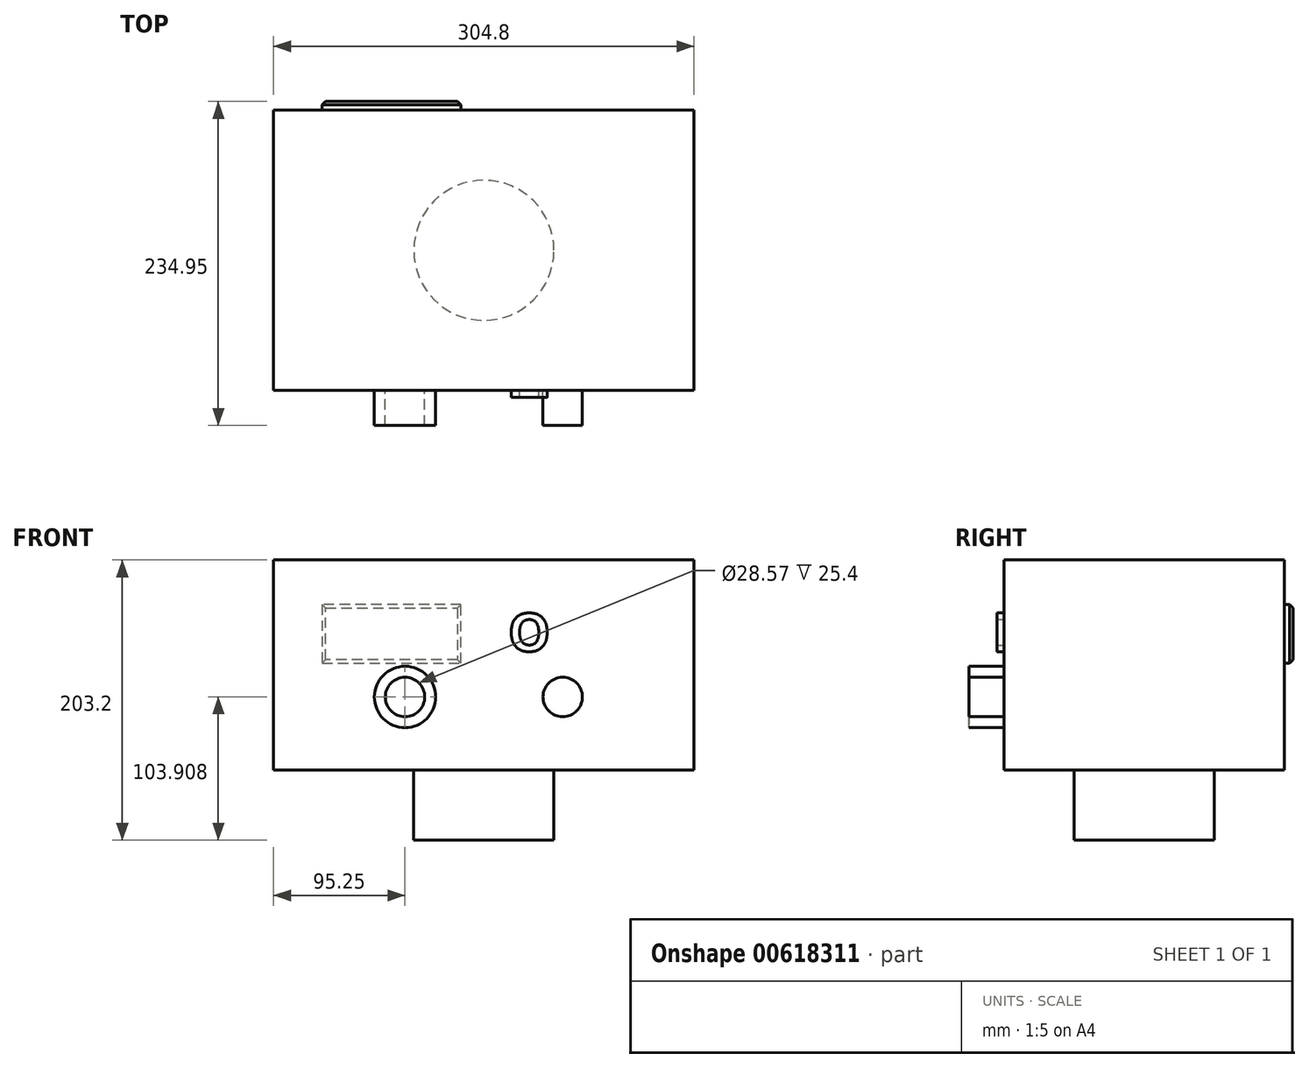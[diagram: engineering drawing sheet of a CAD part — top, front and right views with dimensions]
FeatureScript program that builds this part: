
annotation { "Feature Type Name" : "Feature", "Feature Type Description" : "" }
export const myFeature = defineFeature(function(context is Context, id is Id, definition is map)
    precondition{}
    {
        {
            var Q0;
            Q0=qCreatedBy(makeId("Top.planeOp"),FACE);
            var sketch = newSketch(context, id + "F0", { "sketchPlane" : qUnion([Q0])});
            skLineSegment(sketch, "E0", {"start": v(0, 0) * mm, "end": v(152.4, 0) * mm});
            skLineSegment(sketch, "E1", {"start": v(0, 0) * mm, "end": v(0, 101.6) * mm});
            skLineSegment(sketch, "E2", {"start": v(0, 0) * mm, "end": v(0, -101.6) * mm});
            skLineSegment(sketch, "E3", {"start": v(0, 101.6) * mm, "end": v(152.4, 101.6) * mm});
            skLineSegment(sketch, "E4", {"start": v(0, 0) * mm, "end": v(36.33, -35.5) * mm});
            skCircle(sketch, "E5", {"center": v(0, 0) * mm, "radius": 50.8 * mm});
            skLineSegment(sketch, "E6.bottom", {"start": v(152.4, 101.6) * mm, "end": v(-152.4, 101.6) * mm});
            skLineSegment(sketch, "E6.top", {"start": v(152.4, -101.6) * mm, "end": v(-152.4, -101.6) * mm});
            skLineSegment(sketch, "E6.left", {"start": v(152.4, 101.6) * mm, "end": v(152.4, -101.6) * mm});
            skLineSegment(sketch, "E6.right", {"start": v(-152.4, 101.6) * mm, "end": v(-152.4, -101.6) * mm});
            skSolve(sketch);
        }
        {
            var Q0;
            {var subQ4=sQuery(id+"F0.wireOp",EDGE,"E0");var subQ8=sQuery(id+"F0.wireOp",EDGE,"E6.left");var subQ9=makeQuery(id+"F0.imprint","INTERSECT",VERTEX,{"derivedFrom":[subQ4,subQ8]});Q0=makeQuery(id+"F0.imprint","IMPRINT",FACE,{"disambiguationData":[TD([[makeQuery(id+"F0.imprint","IMPRINT",EDGE,{"disambiguationData":[TD([[subQ9,1.0]])],"derivedFrom":subQ4}),-1.0]])]});}
            var Q1;
            {var subQ1=sQuery(id+"F0.wireOp",EDGE,"E0");var subQ7=sQuery(id+"F0.wireOp",EDGE,"E6.left");var subQ9=makeQuery(id+"F0.imprint","INTERSECT",VERTEX,{"derivedFrom":[subQ1,subQ7]});Q1=makeQuery(id+"F0.imprint","IMPRINT",FACE,{"disambiguationData":[TD([[makeQuery(id+"F0.imprint","IMPRINT",EDGE,{"disambiguationData":[TD([[subQ9,1.0]])],"derivedFrom":subQ1}),1.0]])]});}
            var Q2;
            {var subQ3=sQuery(id+"F0.wireOp",EDGE,"E6.right");Q2=makeQuery(id+"F0.imprint","IMPRINT",FACE,{"disambiguationData":[TD([[makeQuery(id+"F0.imprint","IMPRINT",EDGE,{"derivedFrom":subQ3}),1.0]])]});}
            var Q3;
            {var subQ1=sQuery(id+"F0.wireOp",EDGE,"E1");var subQ3=sQuery(id+"F0.wireOp",EDGE,"E5");var subQ4=makeQuery(id+"F0.imprint","INTERSECT",VERTEX,{"derivedFrom":[subQ1,subQ3]});Q3=makeQuery(id+"F0.imprint","IMPRINT",FACE,{"disambiguationData":[TD([[makeQuery(id+"F0.imprint","IMPRINT",EDGE,{"disambiguationData":[TD([[subQ4,-1.0]])],"derivedFrom":subQ3}),1.0]])]});}
            var Q4;
            {var subQ1=sQuery(id+"F0.wireOp",EDGE,"E0");var subQ3=sQuery(id+"F0.wireOp",EDGE,"E5");var subQ4=makeQuery(id+"F0.imprint","INTERSECT",VERTEX,{"derivedFrom":[subQ1,subQ3]});Q4=makeQuery(id+"F0.imprint","IMPRINT",FACE,{"disambiguationData":[TD([[makeQuery(id+"F0.imprint","IMPRINT",EDGE,{"disambiguationData":[TD([[subQ4,-1.0]])],"derivedFrom":subQ3}),1.0]])]});}
            var Q5;
            {var subQ0=sQuery(id+"F0.wireOp",EDGE,"E4");Q5=makeQuery(id+"F0.imprint","IMPRINT",FACE,{"disambiguationData":[TD([[makeQuery(id+"F0.imprint","IMPRINT",EDGE,{"derivedFrom":subQ0}),-1.0]])]});}
            var Q6;
            {var subQ0=sQuery(id+"F0.wireOp",EDGE,"E4");Q6=makeQuery(id+"F0.imprint","IMPRINT",FACE,{"disambiguationData":[TD([[makeQuery(id+"F0.imprint","IMPRINT",EDGE,{"derivedFrom":subQ0}),1.0]])]});}
            extrude(context, id + "F1", {"entities" : qUnion([Q0, Q1, Q2, Q3, Q4, Q5, Q6]), "depth" : 152.4 * mm, "offsetDistance" : 25.4 * mm});
        }
        {
            var Q0;
            {var subQ0=sQuery(id+"F0.wireOp",EDGE,"E4");Q0=makeQuery(id+"F0.imprint","IMPRINT",FACE,{"disambiguationData":[TD([[makeQuery(id+"F0.imprint","IMPRINT",EDGE,{"derivedFrom":subQ0}),-1.0]])]});}
            var Q1;
            {var subQ0=sQuery(id+"F0.wireOp",EDGE,"E4");Q1=makeQuery(id+"F0.imprint","IMPRINT",FACE,{"disambiguationData":[TD([[makeQuery(id+"F0.imprint","IMPRINT",EDGE,{"derivedFrom":subQ0}),1.0]])]});}
            var Q2;
            {var subQ1=sQuery(id+"F0.wireOp",EDGE,"E0");var subQ3=sQuery(id+"F0.wireOp",EDGE,"E5");var subQ4=makeQuery(id+"F0.imprint","INTERSECT",VERTEX,{"derivedFrom":[subQ1,subQ3]});Q2=makeQuery(id+"F0.imprint","IMPRINT",FACE,{"disambiguationData":[TD([[makeQuery(id+"F0.imprint","IMPRINT",EDGE,{"disambiguationData":[TD([[subQ4,-1.0]])],"derivedFrom":subQ3}),1.0]])]});}
            var Q3;
            {var subQ1=sQuery(id+"F0.wireOp",EDGE,"E1");var subQ3=sQuery(id+"F0.wireOp",EDGE,"E5");var subQ4=makeQuery(id+"F0.imprint","INTERSECT",VERTEX,{"derivedFrom":[subQ1,subQ3]});Q3=makeQuery(id+"F0.imprint","IMPRINT",FACE,{"disambiguationData":[TD([[makeQuery(id+"F0.imprint","IMPRINT",EDGE,{"disambiguationData":[TD([[subQ4,-1.0]])],"derivedFrom":subQ3}),1.0]])]});}
            extrude(context, id + "F2", {"entities" : qUnion([Q0, Q1, Q2, Q3]), "operationType" : NewBodyOperationType.ADD, "oppositeDirection" : true, "depth" : 50.8 * mm, "offsetDistance" : 25.4 * mm});
        }
        {
            var Q0;
            Q0=makeQuery(id+"F1.opExtrude","SWEPT_FACE",FACE,{"disambiguationData":[OSD([sQuery(id+"F0.wireOp",EDGE,"E6.top")])]});
            var sketch = newSketch(context, id + "F3", { "sketchPlane" : qUnion([Q0])});
            skLineSegment(sketch, "E7", {"start": v(152.4, 0) * mm, "end": v(152.4, 53.1) * mm});
            skLineSegment(sketch, "E8", {"start": v(152.4, 53.1) * mm, "end": v(-152.4, 53.1) * mm});
            skLineSegment(sketch, "E9", {"start": v(-152.4, 53.1) * mm, "end": v(-57.15, 53.1) * mm});
            skLineSegment(sketch, "E10", {"start": v(152.4, 53.1) * mm, "end": v(57.15, 53.1) * mm});
            skCircle(sketch, "E11", {"center": v(-57.15, 53.1) * mm, "radius": 22.23 * mm});
            skCircle(sketch, "E12", {"center": v(57.15, 53.1) * mm, "radius": 22.23 * mm});
            skCircle(sketch, "E13", {"center": v(-57.15, 53.1) * mm, "radius": 14.29 * mm});
            skCircle(sketch, "E14", {"center": v(57.15, 53.1) * mm, "radius": 14.29 * mm});
            skSolve(sketch);
        }
        {
            var Q0;
            {var subQ0=sQuery(id+"F3.wireOp",EDGE,"E14");var subQ1=sQuery(id+"F3.wireOp",EDGE,"E8");var subQ2=makeQuery(id+"F3.imprint","INTERSECT",VERTEX,{"derivedFrom":[subQ1,subQ0]});Q0=makeQuery(id+"F3.imprint","IMPRINT",FACE,{"disambiguationData":[TD([[makeQuery(id+"F3.imprint","IMPRINT",EDGE,{"disambiguationData":[TD([[subQ2,-1.0]])],"derivedFrom":subQ1}),-1.0]])]});}
            var Q1;
            {var subQ0=sQuery(id+"F3.wireOp",EDGE,"E14");var subQ1=sQuery(id+"F3.wireOp",EDGE,"E8");var subQ2=makeQuery(id+"F3.imprint","INTERSECT",VERTEX,{"derivedFrom":[subQ1,subQ0]});Q1=makeQuery(id+"F3.imprint","IMPRINT",FACE,{"disambiguationData":[TD([[makeQuery(id+"F3.imprint","IMPRINT",EDGE,{"disambiguationData":[TD([[subQ2,-1.0]])],"derivedFrom":subQ1}),1.0]])]});}
            var Q2;
            {var subQ0=sQuery(id+"F3.wireOp",EDGE,"E11");var subQ1=sQuery(id+"F3.wireOp",EDGE,"E8");var subQ2=makeQuery(id+"F3.imprint","INTERSECT",VERTEX,{"derivedFrom":[subQ1,subQ0]});Q2=makeQuery(id+"F3.imprint","IMPRINT",FACE,{"disambiguationData":[TD([[makeQuery(id+"F3.imprint","IMPRINT",EDGE,{"disambiguationData":[TD([[subQ2,-1.0]])],"derivedFrom":subQ1}),-1.0]])]});}
            var Q3;
            {var subQ0=sQuery(id+"F3.wireOp",EDGE,"E11");var subQ1=sQuery(id+"F3.wireOp",EDGE,"E8");var subQ2=makeQuery(id+"F3.imprint","INTERSECT",VERTEX,{"derivedFrom":[subQ1,subQ0]});Q3=makeQuery(id+"F3.imprint","IMPRINT",FACE,{"disambiguationData":[TD([[makeQuery(id+"F3.imprint","IMPRINT",EDGE,{"disambiguationData":[TD([[subQ2,-1.0]])],"derivedFrom":subQ1}),1.0]])]});}
            var Q4;
            Q4=sQuery(id+"F3.wireOp",EDGE,"E12");
            var Q5;
            Q5=sQuery(id+"F3.wireOp",EDGE,"E14");
            var Q6;
            Q6=sQuery(id+"F3.wireOp",EDGE,"E11");
            var Q7;
            Q7=sQuery(id+"F3.wireOp",EDGE,"E13");
            extrude(context, id + "F4", {"entities" : qUnion([Q0, Q1, Q2, Q3]), "operationType" : NewBodyOperationType.ADD, "surfaceEntities" : qUnion([Q4, Q5, Q6, Q7]), "depth" : 25.4 * mm, "offsetDistance" : 25.4 * mm});
        }
        {
            var Q0;
            Q0=makeQuery(id+"F1.opExtrude","SWEPT_FACE",FACE,{"disambiguationData":[OSD([sQuery(id+"F0.wireOp",EDGE,"E6.bottom")])]});
            var sketch = newSketch(context, id + "F5", { "sketchPlane" : qUnion([Q0])});
            skLineSegment(sketch, "E15.bottom", {"start": v(16.6, 77.64) * mm, "end": v(117.3, 77.64) * mm});
            skLineSegment(sketch, "E15.top", {"start": v(16.6, 120) * mm, "end": v(117.3, 120) * mm});
            skLineSegment(sketch, "E15.left", {"start": v(16.6, 77.64) * mm, "end": v(16.6, 120) * mm});
            skLineSegment(sketch, "E15.right", {"start": v(117.3, 77.64) * mm, "end": v(117.3, 120) * mm});
            skSolve(sketch);
        }
        {
            var Q0;
            Q0=makeQuery(id+"F5.imprint","IMPRINT",FACE,{"disambiguationData":[TD([[makeQuery(id+"F5.imprint","IMPRINT",EDGE,{"derivedFrom":sQuery(id+"F5.wireOp",EDGE,"E15.bottom")}),1.0]])]});
            extrude(context, id + "F6", {"entities" : qUnion([Q0]), "depth" : 6.35 * mm, "offsetDistance" : 25.4 * mm});
        }
        {
            var Q0;
            Q0=makeQuery(id+"F6.opExtrude","CAP_EDGE",EDGE,{"disambiguationData":[OSD([sQuery(id+"F5.wireOp",EDGE,"E15.top")])],"isStart":false});
            var Q1;
            Q1=makeQuery(id+"F6.opExtrude","CAP_EDGE",EDGE,{"disambiguationData":[OSD([sQuery(id+"F5.wireOp",EDGE,"E15.right")])],"isStart":false});
            var Q2;
            Q2=makeQuery(id+"F6.opExtrude","CAP_EDGE",EDGE,{"disambiguationData":[OSD([sQuery(id+"F5.wireOp",EDGE,"E15.left")])],"isStart":false});
            var Q3;
            Q3=makeQuery(id+"F6.opExtrude","CAP_EDGE",EDGE,{"disambiguationData":[OSD([sQuery(id+"F5.wireOp",EDGE,"E15.bottom")])],"isStart":false});
            chamfer(context, id + "F7", {"entities" : qUnion([Q0, Q1, Q2, Q3]), "width" : 2.54 * mm, "tangentPropagation" : true});
        }
        {
            var Q0;
            {var subQ1=sQuery(id+"F0.wireOp",EDGE,"E6.left");var subQ2=sQuery(id+"F0.wireOp",EDGE,"E6.top");Q0=makeQuery(id+"F4.boolean.opBoolean","SPLIT",FACE,{"disambiguationData":[TD([makeQuery(id+"F1.opExtrude","SWEPT_FACE",FACE,{"disambiguationData":[OSD([subQ1])]})])],"derivedFrom":makeQuery(id+"F1.opExtrude","SWEPT_FACE",FACE,{"disambiguationData":[OSD([subQ2])]})});}
            var sketch = newSketch(context, id + "F8", { "sketchPlane" : qUnion([Q0])});
            skText(sketch, "E16", { "text": "OUT", "fontName": "OpenSans-Bold.ttf"});
            const initialGuessF8  = {"E16": [0.0176, 0.08625, 1, 0, 0.0276]};
            skSetInitialGuess(sketch, initialGuessF8);
            skSolve(sketch);
        }
        {
            var Q0;
            Q0=makeQuery(id+"F8.imprint","IMPRINT",FACE,{"disambiguationData":[TD([[makeQuery(id+"F8.imprint","IMPRINT",EDGE,{"derivedFrom":sQuery(id+"F8.wireOp",EDGE,"E16.sketch_text.stroke-0")}),1.0]])]});
            var sketch = newSketch(context, id + "F9", { "sketchPlane" : qUnion([Q0])});
            skSolve(sketch);
        }
        {
            var Q0;
            Q0=qSketchRegion(id+"F9",true);
            var Q1;
            Q1=makeQuery(id+"F9.imprint","IMPRINT",FACE,{"disambiguationData":[TD([[makeQuery(id+"F9.imprint","IMPRINT",EDGE,{"derivedFrom":makeQuery(id+"F8.imprint","IMPRINT",EDGE,{"derivedFrom":sQuery(id+"F8.wireOp",EDGE,"E16.sketch_text.stroke-29")})}),-1.0]])]});
            var Q2;
            Q2=makeQuery(id+"F9.imprint","IMPRINT",FACE,{"disambiguationData":[TD([[makeQuery(id+"F9.imprint","IMPRINT",EDGE,{"derivedFrom":makeQuery(id+"F8.imprint","IMPRINT",EDGE,{"derivedFrom":sQuery(id+"F8.wireOp",EDGE,"E16.sketch_text.stroke-14")})}),-1.0]])]});
            var Q3;
            Q3=makeQuery(id+"F8.imprint","IMPRINT",FACE,{"disambiguationData":[TD([[makeQuery(id+"F8.imprint","IMPRINT",EDGE,{"derivedFrom":sQuery(id+"F8.wireOp",EDGE,"E16.sketch_text.stroke-0")}),-1.0]])]});
            extrude(context, id + "F10", {"entities" : qUnion([Q0, Q1, Q2, Q3]), "operationType" : NewBodyOperationType.ADD, "depth" : 5.08 * mm, "offsetDistance" : 25.4 * mm});
        }
    });
